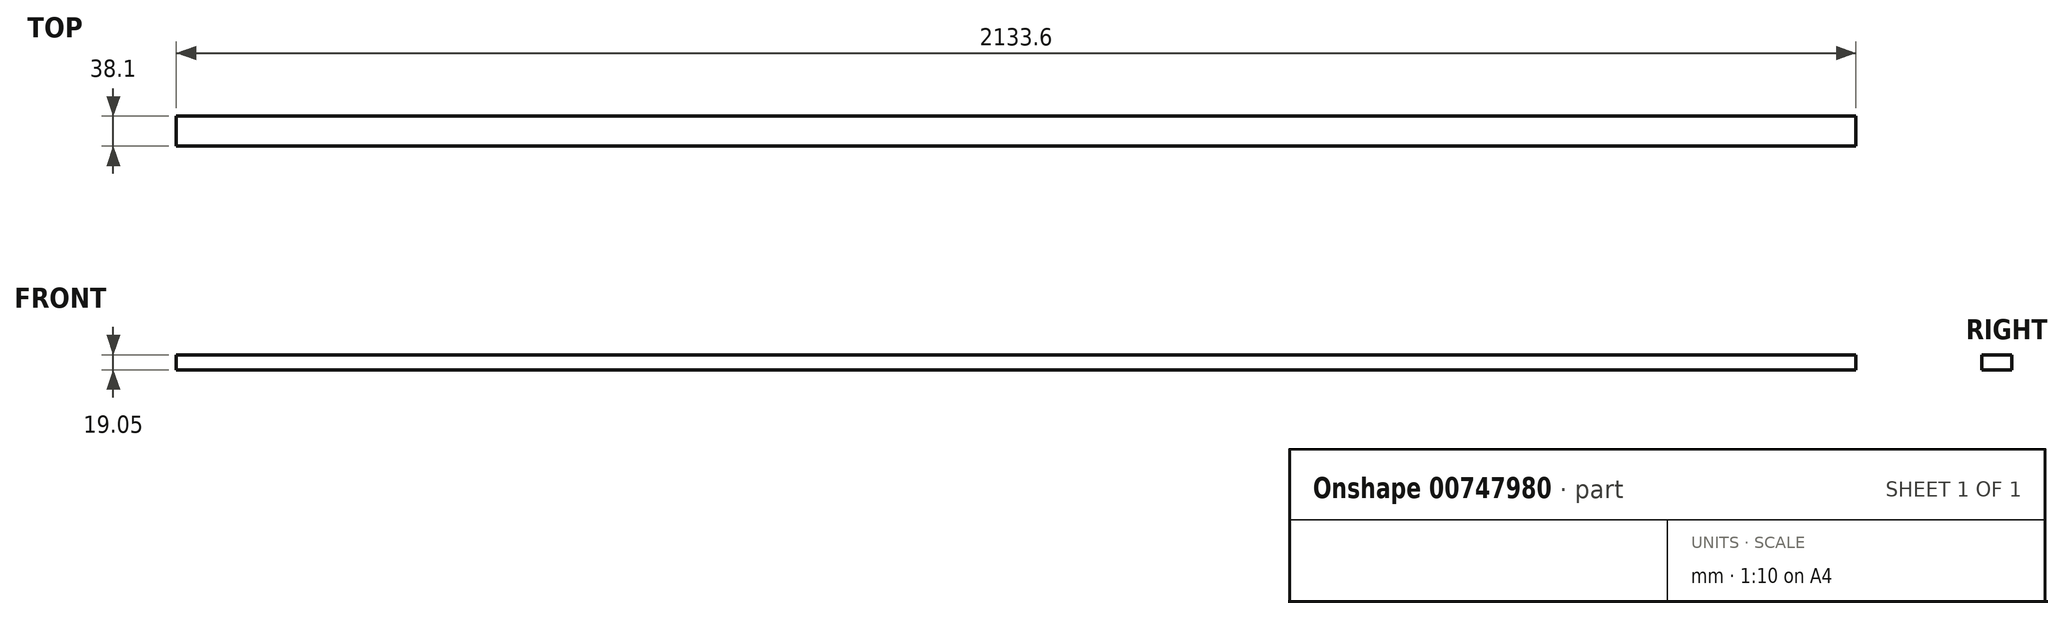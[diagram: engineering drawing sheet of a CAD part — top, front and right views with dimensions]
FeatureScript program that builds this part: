
annotation { "Feature Type Name" : "Feature", "Feature Type Description" : "" }
export const myFeature = defineFeature(function(context is Context, id is Id, definition is map)
    precondition{}
    {
        {
            var Q0;
            Q0=qCreatedBy(makeId("Front.planeOp"),FACE);
            var sketch = newSketch(context, id + "F0", { "sketchPlane" : qUnion([Q0])});
            skLineSegment(sketch, "E0.bottom", {"start": v(-1066.8, -13.62) * mm, "end": v(1066.8, -13.62) * mm});
            skLineSegment(sketch, "E0.top", {"start": v(-1066.8, 5.43) * mm, "end": v(1066.8, 5.43) * mm});
            skLineSegment(sketch, "E0.left", {"start": v(-1066.8, -13.62) * mm, "end": v(-1066.8, 5.43) * mm});
            skLineSegment(sketch, "E0.right", {"start": v(1066.8, -13.62) * mm, "end": v(1066.8, 5.43) * mm});
            skPoint(sketch, "E0.middle", {"position": v(0, -4.1) * mm});
            skSolve(sketch);
        }
        {
            var Q0;
            Q0 = qSketchRegion(id + "F0", true);
            extrude(context, id + "F1", {"entities" : qUnion([Q0]), "depth" : 38.1 * mm, "offsetDistance" : 25.4 * mm});
        }
    });
